# Revit family: RN 17020 Filtro
name_source: partatom
category: Rohrzubehör
units: mm (PartAtom-declared; Revit-internal decimal feet)

## family parameters
Arbeitsebenenbasiert = Nein
Beim Laden mit Abzugskörper schneiden = Nein
Bemaßung runder Anschluss = Durchmesser verwenden
Gemeinsam genutzt = Nein
Immer vertikal = Ja
Teiletyp = Ventil - Zerlegung in

## types (3) — shared parameters
1.010.00.2 Blattnummer der Richtlinie = 17
1.010.00.3 Ausgabedatum (Monat) der Richtlinie = 201601
1.010.00.4 Herstellername = R. Nussbaum AG
1.010.00.5 Revisionsdatum der Datei = 20190528
1.010.00.6 Webadresse des Herstellers = http://www.nussbaum.ch
1.100.00.3 Sortiernummer für Anzeigereihenfolge = 9
1.100.00.4 Produktbezeichnung = Filterkombination, Filter und Schmutzfänger
1.960/3L.00.8 Link (URL) = https://www.nussbaum.ch
17.700.00.4 Armaturentyp = 1
17.700.00.7 Maximale Betriebstemperatur TB [°C] = 40
17.700.00.8 Maximaler Betriebsdruck (Arbeitsdruck) ps [1.0 · 105 Pa] = 16
Connector Visibility = Nein
EnclosingSpace Visibility = Nein
Hersteller = R. Nussbauzm AG
URL = https://www.nussbaum.ch

## per-type parameters (varying)
| type | 1.800.00.3 TGA-Nummer | 1.810.00.3 Hersteller-Bestellnummer | 1.810.00.4 DATANORM-Nummer | 1.810.00.5 StLB-Nummer | 1.810.00.6 GTIN-Nummer | 17.700.00.30 Produktbeschreibung | 17.700.00.5 Nennweite DN | 17.700.00.6 kvs-Wert [m3/h] | CONNECTOR0_DIAMETER_dX_0r | CONNECTOR0_dX_00 | CONNECTOR0_dX_01 | CONNECTOR0_ref_dX | CONNECTOR1_DIAMETER_dX_0r | CONNECTOR1_dX_00 | CONNECTOR1_dX_01 | CONNECTOR1_ref_dX | Modell | R. Nussbaum AG 17020.27 de Visibility | R. Nussbaum AG 17020.28 de Visibility | R. Nussbaum AG 17020.29 de Visibility | Typenkommentare |
| DN 65 | 00900400000000000000000000000300600000000000000001???00000 | 17020.27 | 17020.27 | 716.117 | 7612945003140 | 17020.27, Filter, mit Flanschen, DN=65 | 65 | 85 | 65 mm | 146 mm | 145 mm | 146 mm | 65 mm | 145 mm | 146 mm | 146 mm | 17020.27 | Ja | Nein | Nein | FiltroDN 65 |
| DN 80 | 00900400000000000000000000000300600000000000000002???00000 | 17020.28 | 17020.28 | 716.118 | 7612945003157 | 17020.28, Filter, mit Flanschen, DN=80 | 80 | 109 | 80 mm | 156 mm | 155 mm | 156 mm | 80 mm | 155 mm | 156 mm | 156 mm | 17020.28 | Nein | Ja | Nein | FiltroDN 80 |
| DN 100 | 00900400000000000000000000000300600000000000000003???00000 | 17020.29 | 17020.29 | 716.121 | 7612945003164 | 17020.29, Filter, mit Flanschen, DN=100 | 100 | 215 | 100 mm | 176 mm | 175 mm | 176 mm | 100 mm | 175 mm | 176 mm | 176 mm | 17020.29 | Nein | Nein | Ja | FiltroDN 100 |

## geometry (parser evidence)
native form markers: Sweep x1
no freeform markers — native parametric forms only
